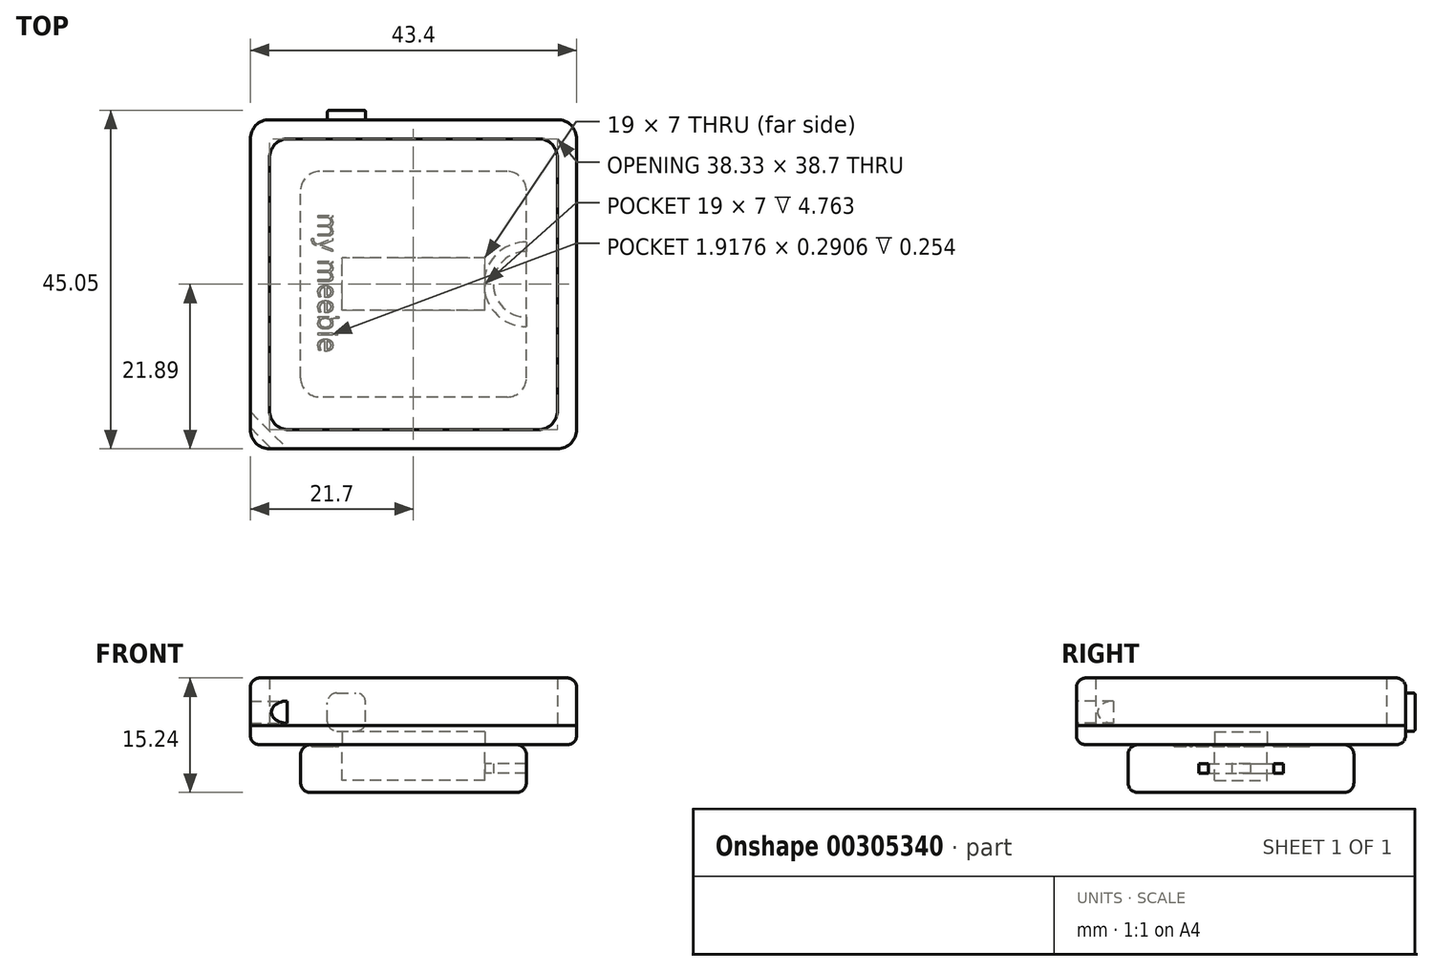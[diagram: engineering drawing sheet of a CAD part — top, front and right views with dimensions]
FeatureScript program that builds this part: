
annotation { "Feature Type Name" : "Feature", "Feature Type Description" : "" }
export const myFeature = defineFeature(function(context is Context, id is Id, definition is map)
    precondition{}
    {
        {
            var Q0;
            Q0=qCreatedBy(makeId("Top.planeOp"),FACE);
            var sketch = newSketch(context, id + "F0", { "sketchPlane" : qUnion([Q0])});
            skPoint(sketch, "E0.middle", {"position": v(0, 0) * mm});
            skLineSegment(sketch, "E1.bottom", {"start": v(19.05, -19.06) * mm, "end": v(-19.05, -19.06) * mm});
            skLineSegment(sketch, "E1.top", {"start": v(19.05, 19.06) * mm, "end": v(-19.05, 19.06) * mm});
            skLineSegment(sketch, "E1.left", {"start": v(19.05, -19.06) * mm, "end": v(19.05, 19.06) * mm});
            skLineSegment(sketch, "E1.right", {"start": v(-19.05, -19.06) * mm, "end": v(-19.05, 19.06) * mm});
            skSolve(sketch);
        }
        {
            var Q0;
            Q0=makeQuery(id+"F0.imprint","IMPRINT",FACE,{"disambiguationData":[TD([[makeQuery(id+"F0.imprint","IMPRINT",EDGE,{"derivedFrom":sQuery(id+"F0.wireOp",EDGE,"E1.bottom")}),-1.0]])]});
            extrude(context, id + "F1", {"entities" : qUnion([Q0]), "depth" : 6.35 * mm});
        }
        {
            var Q0;
            Q0=makeQuery(id+"F1.opExtrude","SWEPT_EDGE",EDGE,{"disambiguationData":[OSD([sQuery(id+"F0.wireOp",EDGE,"E1.top"),sQuery(id+"F0.wireOp",EDGE,"E1.right")])]});
            var Q1;
            Q1=makeQuery(id+"F1.opExtrude","SWEPT_EDGE",EDGE,{"disambiguationData":[OSD([sQuery(id+"F0.wireOp",EDGE,"E1.top"),sQuery(id+"F0.wireOp",EDGE,"E1.left")])]});
            var Q2;
            Q2=makeQuery(id+"F1.opExtrude","SWEPT_EDGE",EDGE,{"disambiguationData":[OSD([sQuery(id+"F0.wireOp",EDGE,"E1.bottom"),sQuery(id+"F0.wireOp",EDGE,"E1.right")])]});
            var Q3;
            Q3=makeQuery(id+"F1.opExtrude","SWEPT_EDGE",EDGE,{"disambiguationData":[OSD([sQuery(id+"F0.wireOp",EDGE,"E1.bottom"),sQuery(id+"F0.wireOp",EDGE,"E1.left")])]});
            fillet(context, id + "F2", {"entities" : qUnion([Q0, Q1, Q2, Q3]), "radius" : 2.54 * mm, "tangentPropagation" : true, "allowEdgeOverflow" : false});
        }
        {
            var Q0;
            Q0=makeQuery(id+"F1.opExtrude","CAP_FACE",FACE,{"disambiguationData":[OSD([sQuery(id+"F0.wireOp",EDGE,"E1.bottom"),sQuery(id+"F0.wireOp",EDGE,"E1.top"),sQuery(id+"F0.wireOp",EDGE,"E1.left"),sQuery(id+"F0.wireOp",EDGE,"E1.right")])],"isStart":true});
            var sketch = newSketch(context, id + "F3", { "sketchPlane" : qUnion([Q0])});
            skLineSegment(sketch, "E2.bottom", {"start": v(21.7, 21.89) * mm, "end": v(-21.7, 21.89) * mm});
            skLineSegment(sketch, "E2.top", {"start": v(21.7, -21.89) * mm, "end": v(-21.7, -21.89) * mm});
            skLineSegment(sketch, "E2.left", {"start": v(21.7, 21.89) * mm, "end": v(21.7, -21.89) * mm});
            skLineSegment(sketch, "E2.right", {"start": v(-21.7, 21.89) * mm, "end": v(-21.7, -21.89) * mm});
            skPoint(sketch, "E2.middle", {"position": v(0, 0) * mm});
            skSolve(sketch);
        }
        {
            var Q0;
            Q0 = qSketchRegion(id + "F3", true);
            extrude(context, id + "F4", {"entities" : qUnion([Q0]), "depth" : 2.54 * mm});
        }
        {
            var Q0;
            Q0=makeQuery(id+"F4.opExtrude","SWEPT_EDGE",EDGE,{"disambiguationData":[OSD([sQuery(id+"F3.wireOp",EDGE,"E2.bottom"),sQuery(id+"F3.wireOp",EDGE,"E2.right")])]});
            var Q1;
            Q1=makeQuery(id+"F4.opExtrude","SWEPT_EDGE",EDGE,{"disambiguationData":[OSD([sQuery(id+"F3.wireOp",EDGE,"E2.bottom"),sQuery(id+"F3.wireOp",EDGE,"E2.left")])]});
            var Q2;
            Q2=makeQuery(id+"F4.opExtrude","SWEPT_EDGE",EDGE,{"disambiguationData":[OSD([sQuery(id+"F3.wireOp",EDGE,"E2.top"),sQuery(id+"F3.wireOp",EDGE,"E2.left")])]});
            var Q3;
            Q3=makeQuery(id+"F4.opExtrude","SWEPT_EDGE",EDGE,{"disambiguationData":[OSD([sQuery(id+"F3.wireOp",EDGE,"E2.top"),sQuery(id+"F3.wireOp",EDGE,"E2.right")])]});
            fillet(context, id + "F5", {"entities" : qUnion([Q0, Q1, Q2, Q3]), "radius" : 2.54 * mm, "tangentPropagation" : true, "allowEdgeOverflow" : false});
        }
        {
            var Q0;
            Q0=makeQuery(id+"F4.opExtrude","CAP_FACE",FACE,{"disambiguationData":[OSD([sQuery(id+"F3.wireOp",EDGE,"E2.bottom"),sQuery(id+"F3.wireOp",EDGE,"E2.top"),sQuery(id+"F3.wireOp",EDGE,"E2.left"),sQuery(id+"F3.wireOp",EDGE,"E2.right")])],"isStart":true});
            var sketch = newSketch(context, id + "F6", { "sketchPlane" : qUnion([Q0])});
            skLineSegment(sketch, "E3.bottom", {"start": v(21.7, 21.89) * mm, "end": v(-21.7, 21.89) * mm});
            skLineSegment(sketch, "E3.top", {"start": v(21.7, -21.89) * mm, "end": v(-21.7, -21.89) * mm});
            skLineSegment(sketch, "E3.left", {"start": v(21.7, 21.89) * mm, "end": v(21.7, -21.89) * mm});
            skLineSegment(sketch, "E3.right", {"start": v(-21.7, 21.89) * mm, "end": v(-21.7, -21.89) * mm});
            skPoint(sketch, "E3.middle", {"position": v(0, 0) * mm});
            skLineSegment(sketch, "E4.bottom", {"start": v(19.16, 19.35) * mm, "end": v(-19.16, 19.35) * mm});
            skLineSegment(sketch, "E4.top", {"start": v(19.16, -19.35) * mm, "end": v(-19.16, -19.35) * mm});
            skLineSegment(sketch, "E4.left", {"start": v(19.16, 19.35) * mm, "end": v(19.16, -19.35) * mm});
            skLineSegment(sketch, "E4.right", {"start": v(-19.16, 19.35) * mm, "end": v(-19.16, -19.35) * mm});
            skSolve(sketch);
        }
        {
            var Q0;
            Q0 = qSketchRegion(id + "F6", true);
            extrude(context, id + "F7", {"entities" : qUnion([Q0]), "depth" : 6.35 * mm});
        }
        {
            var Q0;
            Q0=makeQuery(id+"F7.opExtrude","SWEPT_EDGE",EDGE,{"disambiguationData":[OSD([sQuery(id+"F6.wireOp",EDGE,"E3.bottom"),sQuery(id+"F6.wireOp",EDGE,"E3.right")])]});
            var Q1;
            Q1=makeQuery(id+"F7.opExtrude","SWEPT_EDGE",EDGE,{"disambiguationData":[OSD([sQuery(id+"F6.wireOp",EDGE,"E3.top"),sQuery(id+"F6.wireOp",EDGE,"E3.right")])]});
            var Q2;
            Q2=makeQuery(id+"F7.opExtrude","SWEPT_EDGE",EDGE,{"disambiguationData":[OSD([sQuery(id+"F6.wireOp",EDGE,"E3.top"),sQuery(id+"F6.wireOp",EDGE,"E3.left")])]});
            var Q3;
            Q3=makeQuery(id+"F7.opExtrude","SWEPT_EDGE",EDGE,{"disambiguationData":[OSD([sQuery(id+"F6.wireOp",EDGE,"E3.bottom"),sQuery(id+"F6.wireOp",EDGE,"E3.left")])]});
            var Q4;
            Q4=makeQuery(id+"F7.opExtrude","SWEPT_EDGE",EDGE,{"disambiguationData":[OSD([sQuery(id+"F6.wireOp",EDGE,"E4.top"),sQuery(id+"F6.wireOp",EDGE,"E4.left")])]});
            var Q5;
            Q5=makeQuery(id+"F7.opExtrude","SWEPT_EDGE",EDGE,{"disambiguationData":[OSD([sQuery(id+"F6.wireOp",EDGE,"E4.bottom"),sQuery(id+"F6.wireOp",EDGE,"E4.right")])]});
            var Q6;
            Q6=makeQuery(id+"F7.opExtrude","SWEPT_EDGE",EDGE,{"disambiguationData":[OSD([sQuery(id+"F6.wireOp",EDGE,"E4.top"),sQuery(id+"F6.wireOp",EDGE,"E4.right")])]});
            var Q7;
            Q7=makeQuery(id+"F7.opExtrude","SWEPT_EDGE",EDGE,{"disambiguationData":[OSD([sQuery(id+"F6.wireOp",EDGE,"E4.bottom"),sQuery(id+"F6.wireOp",EDGE,"E4.left")])]});
            fillet(context, id + "F8", {"entities" : qUnion([Q0, Q1, Q2, Q3, Q4, Q5, Q6, Q7]), "radius" : 2.54 * mm, "tangentPropagation" : true, "allowEdgeOverflow" : false});
        }
        {
            var Q0;
            Q0=makeQuery(id+"F7.opExtrude","CAP_EDGE",EDGE,{"disambiguationData":[OSD([sQuery(id+"F6.wireOp",EDGE,"E3.right")])],"isStart":false});
            var Q1;
            Q1=makeQuery(id+"F4.opExtrude","CAP_EDGE",EDGE,{"disambiguationData":[OSD([sQuery(id+"F3.wireOp",EDGE,"E2.top")])],"isStart":false});
            fillet(context, id + "F9", {"entities" : qUnion([Q0, Q1]), "radius" : 1.27 * mm, "tangentPropagation" : true, "allowEdgeOverflow" : false});
        }
        {
            var Q0;
            Q0=qCreatedBy(makeId("Right.planeOp"),FACE);
            var Q1;
            Q1=qCreatedBy(makeId("Front.planeOp"),FACE);
            cPlane(context, id + "F10", {"entities" : qUnion([Q0, Q1]), "cplaneType" : CPlaneType.MID_PLANE, "offset" : 25.4 * mm, "flipAlignment" : true, "width" : 152.4 * mm, "height" : 152.4 * mm});
        }
        {
            var Q0;
            Q0=qCreatedBy(id+"F10.planeOp",FACE);
            var sketch = newSketch(context, id + "F11", { "sketchPlane" : qUnion([Q0])});
            skArc(sketch, "E5", {"start": v(-27.34, 3.3) * mm, "mid": v(-28.82, 1.8) * mm, "end": v(-27.34, 0.32) * mm});
            skLineSegment(sketch, "E6", {"start": v(-27.34, 3.3) * mm, "end": v(-27.34, 0.32) * mm});
            skSolve(sketch);
        }
        {
            var Q0;
            Q0 = qSketchRegion(id + "F11", true);
            extrude(context, id + "F12", {"entities" : qUnion([Q0]), "operationType" : NewBodyOperationType.REMOVE, "endBound" : BoundingType.SYMMETRIC, "oppositeDirection" : true, "depth" : 25.4 * mm});
        }
        {
            var Q0;
            Q0=makeQuery(id+"F4.opExtrude","CAP_FACE",FACE,{"disambiguationData":[OSD([sQuery(id+"F3.wireOp",EDGE,"E2.bottom"),sQuery(id+"F3.wireOp",EDGE,"E2.top"),sQuery(id+"F3.wireOp",EDGE,"E2.left"),sQuery(id+"F3.wireOp",EDGE,"E2.right")])],"isStart":false});
            var sketch = newSketch(context, id + "F13", { "sketchPlane" : qUnion([Q0])});
            skLineSegment(sketch, "E7.bottom", {"start": v(9.5, 3.5) * mm, "end": v(-9.5, 3.5) * mm});
            skLineSegment(sketch, "E7.top", {"start": v(9.5, -3.5) * mm, "end": v(-9.5, -3.5) * mm});
            skLineSegment(sketch, "E7.left", {"start": v(9.5, 3.5) * mm, "end": v(9.5, -3.5) * mm});
            skLineSegment(sketch, "E7.right", {"start": v(-9.5, 3.5) * mm, "end": v(-9.5, -3.5) * mm});
            skPoint(sketch, "E7.middle", {"position": v(0, 0) * mm});
            skSolve(sketch);
        }
        {
            var Q0;
            Q0 = qSketchRegion(id + "F13", true);
            extrude(context, id + "F14", {"entities" : qUnion([Q0]), "operationType" : NewBodyOperationType.REMOVE, "oppositeDirection" : true, "depth" : 1.75 * mm});
        }
        {
            var Q0;
            Q0=makeQuery(id+"F7.opExtrude","SWEPT_FACE",FACE,{"disambiguationData":[OSD([sQuery(id+"F6.wireOp",EDGE,"E3.bottom")])]});
            var sketch = newSketch(context, id + "F15", { "sketchPlane" : qUnion([Q0])});
            skLineSegment(sketch, "E8.bottom", {"start": v(11.44, -0.73) * mm, "end": v(6.36, -0.73) * mm});
            skLineSegment(sketch, "E8.top", {"start": v(11.44, 4.35) * mm, "end": v(6.36, 4.35) * mm});
            skLineSegment(sketch, "E8.left", {"start": v(11.44, -0.73) * mm, "end": v(11.44, 4.35) * mm});
            skLineSegment(sketch, "E8.right", {"start": v(6.36, -0.73) * mm, "end": v(6.36, 4.35) * mm});
            skPoint(sketch, "E8.middle", {"position": v(8.9, 1.81) * mm});
            skSolve(sketch);
        }
        {
            var Q0;
            Q0 = qSketchRegion(id + "F15", true);
            extrude(context, id + "F16", {"entities" : qUnion([Q0]), "depth" : 1.27 * mm});
        }
        {
            var Q0;
            Q0=makeQuery(id+"F16.opExtrude","SWEPT_EDGE",EDGE,{"disambiguationData":[OSD([sQuery(id+"F15.wireOp",EDGE,"E8.bottom"),sQuery(id+"F15.wireOp",EDGE,"E8.left")])]});
            var Q1;
            Q1=makeQuery(id+"F16.opExtrude","SWEPT_EDGE",EDGE,{"disambiguationData":[OSD([sQuery(id+"F15.wireOp",EDGE,"E8.top"),sQuery(id+"F15.wireOp",EDGE,"E8.left")])]});
            var Q2;
            Q2=makeQuery(id+"F16.opExtrude","SWEPT_EDGE",EDGE,{"disambiguationData":[OSD([sQuery(id+"F15.wireOp",EDGE,"E8.bottom"),sQuery(id+"F15.wireOp",EDGE,"E8.right")])]});
            var Q3;
            Q3=makeQuery(id+"F16.opExtrude","SWEPT_EDGE",EDGE,{"disambiguationData":[OSD([sQuery(id+"F15.wireOp",EDGE,"E8.top"),sQuery(id+"F15.wireOp",EDGE,"E8.right")])]});
            fillet(context, id + "F17", {"entities" : qUnion([Q0, Q1, Q2, Q3]), "radius" : 1.27 * mm, "tangentPropagation" : true, "allowEdgeOverflow" : false});
        }
        {
            var Q0;
            Q0=makeQuery(id+"F16.opExtrude","CAP_FACE",FACE,{"disambiguationData":[OSD([sQuery(id+"F15.wireOp",EDGE,"E8.bottom"),sQuery(id+"F15.wireOp",EDGE,"E8.top"),sQuery(id+"F15.wireOp",EDGE,"E8.left"),sQuery(id+"F15.wireOp",EDGE,"E8.right")])],"isStart":false});
            fillet(context, id + "F18", {"entities" : qUnion([Q0]), "radius" : 0.25 * mm, "tangentPropagation" : true, "allowEdgeOverflow" : false});
        }
        {
            var Q0;
            Q0=makeQuery(id+"F1.opExtrude","SWEPT_BODY",BODY,{"disambiguationData":[OSD([sQuery(id+"F0.wireOp",EDGE,"E1.bottom"),sQuery(id+"F0.wireOp",EDGE,"E1.top"),sQuery(id+"F0.wireOp",EDGE,"E1.left"),sQuery(id+"F0.wireOp",EDGE,"E1.right")])]});
            deleteBodies(context, id + "F19", {"entities" : qUnion([Q0])});
        }
        {
            var Q0;
            Q0=makeQuery(id+"F4.opExtrude","CAP_FACE",FACE,{"disambiguationData":[OSD([sQuery(id+"F3.wireOp",EDGE,"E2.bottom"),sQuery(id+"F3.wireOp",EDGE,"E2.top"),sQuery(id+"F3.wireOp",EDGE,"E2.left"),sQuery(id+"F3.wireOp",EDGE,"E2.right")])],"isStart":false});
            var sketch = newSketch(context, id + "F20", { "sketchPlane" : qUnion([Q0])});
            skLineSegment(sketch, "E9.bottom", {"start": v(12.46, 15) * mm, "end": v(-12.46, 15) * mm});
            skLineSegment(sketch, "E9.top", {"start": v(12.46, -15) * mm, "end": v(-12.46, -15) * mm});
            skLineSegment(sketch, "E9.left", {"start": v(15, 12.46) * mm, "end": v(15, -12.46) * mm});
            skLineSegment(sketch, "E9.right", {"start": v(-15, 12.46) * mm, "end": v(-15, -12.46) * mm});
            skPoint(sketch, "E9.middle", {"position": v(0, 0) * mm});
            skPoint(sketch, "E10.visualSharp", {"position": v(-15, 15) * mm});
            skArc(sketch, "E10.filletArc", {"start": v(-12.46, 15) * mm, "mid": v(-14.26, 14.26) * mm, "end": v(-15, 12.46) * mm});
            skPoint(sketch, "E11.visualSharp", {"position": v(15, 15) * mm});
            skArc(sketch, "E11.filletArc", {"start": v(15, 12.46) * mm, "mid": v(14.26, 14.26) * mm, "end": v(12.46, 15) * mm});
            skPoint(sketch, "E12.visualSharp", {"position": v(15, -15) * mm});
            skArc(sketch, "E12.filletArc", {"start": v(12.46, -15) * mm, "mid": v(14.26, -14.26) * mm, "end": v(15, -12.46) * mm});
            skPoint(sketch, "E13.visualSharp", {"position": v(-15, -15) * mm});
            skArc(sketch, "E13.filletArc", {"start": v(-15, -12.46) * mm, "mid": v(-14.26, -14.26) * mm, "end": v(-12.46, -15) * mm});
            skSolve(sketch);
        }
        {
            var Q0;
            Q0=makeQuery(id+"F20.imprint","IMPRINT",FACE,{"disambiguationData":[TD([[makeQuery(id+"F20.imprint","IMPRINT",EDGE,{"derivedFrom":sQuery(id+"F20.wireOp",EDGE,"E9.bottom")}),1.0]])]});
            extrude(context, id + "F21", {"entities" : qUnion([Q0]), "depth" : 6.35 * mm});
        }
        {
            var Q0;
            Q0=makeQuery(id+"F21.opExtrude","CAP_EDGE",EDGE,{"disambiguationData":[OSD([sQuery(id+"F20.wireOp",EDGE,"E9.bottom")])],"isStart":false});
            var Q1;
            Q1=makeQuery(id+"F21.opExtrude","CAP_EDGE",EDGE,{"disambiguationData":[OSD([sQuery(id+"F20.wireOp",EDGE,"E9.bottom")])],"isStart":true});
            fillet(context, id + "F22", {"entities" : qUnion([Q0, Q1]), "radius" : 1.27 * mm, "tangentPropagation" : true, "allowEdgeOverflow" : false});
        }
        {
            var Q0;
            Q0=makeQuery(id+"F21.opExtrude","CAP_FACE",FACE,{"disambiguationData":[OSD([sQuery(id+"F13.wireOp",EDGE,"E7.bottom"),sQuery(id+"F13.wireOp",EDGE,"E7.top"),sQuery(id+"F13.wireOp",EDGE,"E7.left"),sQuery(id+"F13.wireOp",EDGE,"E7.right"),sQuery(id+"F20.wireOp",EDGE,"E9.bottom"),sQuery(id+"F20.wireOp",EDGE,"E9.top"),sQuery(id+"F20.wireOp",EDGE,"E9.left"),sQuery(id+"F20.wireOp",EDGE,"E9.right"),sQuery(id+"F20.wireOp",EDGE,"E10.filletArc"),sQuery(id+"F20.wireOp",EDGE,"E11.filletArc"),sQuery(id+"F20.wireOp",EDGE,"E12.filletArc"),sQuery(id+"F20.wireOp",EDGE,"E13.filletArc")])],"isStart":false});
            var sketch = newSketch(context, id + "F23", { "sketchPlane" : qUnion([Q0])});
            skLineSegment(sketch, "E14.bottom", {"start": v(9.5, 3.5) * mm, "end": v(-9.5, 3.5) * mm});
            skLineSegment(sketch, "E14.top", {"start": v(9.5, -3.5) * mm, "end": v(-9.5, -3.5) * mm});
            skLineSegment(sketch, "E14.left", {"start": v(9.5, 3.5) * mm, "end": v(9.5, -3.5) * mm});
            skLineSegment(sketch, "E14.right", {"start": v(-9.5, 3.5) * mm, "end": v(-9.5, -3.5) * mm});
            skPoint(sketch, "E14.middle", {"position": v(0, 0) * mm});
            skSolve(sketch);
        }
        {
            var Q0;
            Q0 = qSketchRegion(id + "F23", true);
            extrude(context, id + "F24", {"entities" : qUnion([Q0]), "operationType" : NewBodyOperationType.ADD, "oppositeDirection" : true, "depth" : 1.59 * mm});
        }
        {
            var Q0;
            Q0=makeQuery(id+"F21.opExtrude","SWEPT_FACE",FACE,{"disambiguationData":[OSD([sQuery(id+"F20.wireOp",EDGE,"E9.left")])]});
            var sketch = newSketch(context, id + "F25", { "sketchPlane" : qUnion([Q0])});
            skLineSegment(sketch, "E15", {"start": v(0, -5.66) * mm, "end": v(5, -5.66) * mm});
            skSolve(sketch);
        }
        {
            var Q0;
            {var subQ0=sQuery(id+"F20.wireOp",EDGE,"E9.left");Q0=makeQuery(id+"F25.imprint","IMPRINT",FACE,{"disambiguationData":[TD([[makeQuery(id+"F25.imprint","IMPRINT",EDGE,{"derivedFrom":makeQuery(id+"F21.opExtrude","SWEPT_EDGE",EDGE,{"disambiguationData":[OSD([subQ0,sQuery(id+"F20.wireOp",EDGE,"E11.filletArc")])]})}),-1.0]])]});}
            var sketch = newSketch(context, id + "F26", { "sketchPlane" : qUnion([Q0])});
            skLineSegment(sketch, "E16.bottom", {"start": v(5.64, -6.3) * mm, "end": v(4.37, -6.3) * mm});
            skLineSegment(sketch, "E16.top", {"start": v(5.64, -5.03) * mm, "end": v(4.37, -5.03) * mm});
            skLineSegment(sketch, "E16.left", {"start": v(5.64, -6.3) * mm, "end": v(5.64, -5.03) * mm});
            skLineSegment(sketch, "E16.right", {"start": v(4.37, -6.3) * mm, "end": v(4.37, -5.03) * mm});
            skPoint(sketch, "E16.middle", {"position": v(5, -5.66) * mm});
            skSolve(sketch);
        }
        {
            var Q0;
            {var subQ0=sQuery(id+"F20.wireOp",EDGE,"E9.left");Q0=makeQuery(id+"F25.imprint","IMPRINT",FACE,{"disambiguationData":[TD([[makeQuery(id+"F25.imprint","IMPRINT",EDGE,{"derivedFrom":makeQuery(id+"F21.opExtrude","SWEPT_EDGE",EDGE,{"disambiguationData":[OSD([subQ0,sQuery(id+"F20.wireOp",EDGE,"E11.filletArc")])]})}),-1.0]])]});}
            var sketch = newSketch(context, id + "F27", { "sketchPlane" : qUnion([Q0])});
            skLineSegment(sketch, "E17", {"start": v(0, 0) * mm, "end": v(0, -10.23) * mm});
            skSolve(sketch);
        }
        {
            var Q0;
            Q0 = qSketchRegion(id + "F26", true);
            var Q1;
            Q1=sQuery(id+"F27.wireOp",EDGE,"E17");
            revolve(context, id + "F28", {"operationType" : NewBodyOperationType.REMOVE, "entities" : qUnion([Q0]), "axis" : qUnion([Q1]), "revolveType" : RevolveType.FULL, "oppositeDirection" : true});
        }
        {
            var Q0;
            Q0=makeQuery(id+"F21.opExtrude","CAP_FACE",FACE,{"disambiguationData":[OSD([sQuery(id+"F13.wireOp",EDGE,"E7.bottom"),sQuery(id+"F13.wireOp",EDGE,"E7.top"),sQuery(id+"F13.wireOp",EDGE,"E7.left"),sQuery(id+"F13.wireOp",EDGE,"E7.right"),sQuery(id+"F20.wireOp",EDGE,"E9.bottom"),sQuery(id+"F20.wireOp",EDGE,"E9.top"),sQuery(id+"F20.wireOp",EDGE,"E9.left"),sQuery(id+"F20.wireOp",EDGE,"E9.right"),sQuery(id+"F20.wireOp",EDGE,"E10.filletArc"),sQuery(id+"F20.wireOp",EDGE,"E11.filletArc"),sQuery(id+"F20.wireOp",EDGE,"E12.filletArc"),sQuery(id+"F20.wireOp",EDGE,"E13.filletArc")])],"isStart":true});
            var sketch = newSketch(context, id + "F29", { "sketchPlane" : qUnion([Q0])});
            skText(sketch, "E18", { "text": "my meebie", "fontName": "OpenSans-Regular.ttf"});
            const initialGuessF29  = {"E18": [-0.01268, 0.00945, 0, -1, 0.00258]};
            skSetInitialGuess(sketch, initialGuessF29);
            skSolve(sketch);
        }
        {
            var Q0;
            Q0 = qSketchRegion(id + "F29", true);
            extrude(context, id + "F30", {"entities" : qUnion([Q0]), "operationType" : NewBodyOperationType.REMOVE, "oppositeDirection" : true, "depth" : 0.25 * mm});
        }
    });
